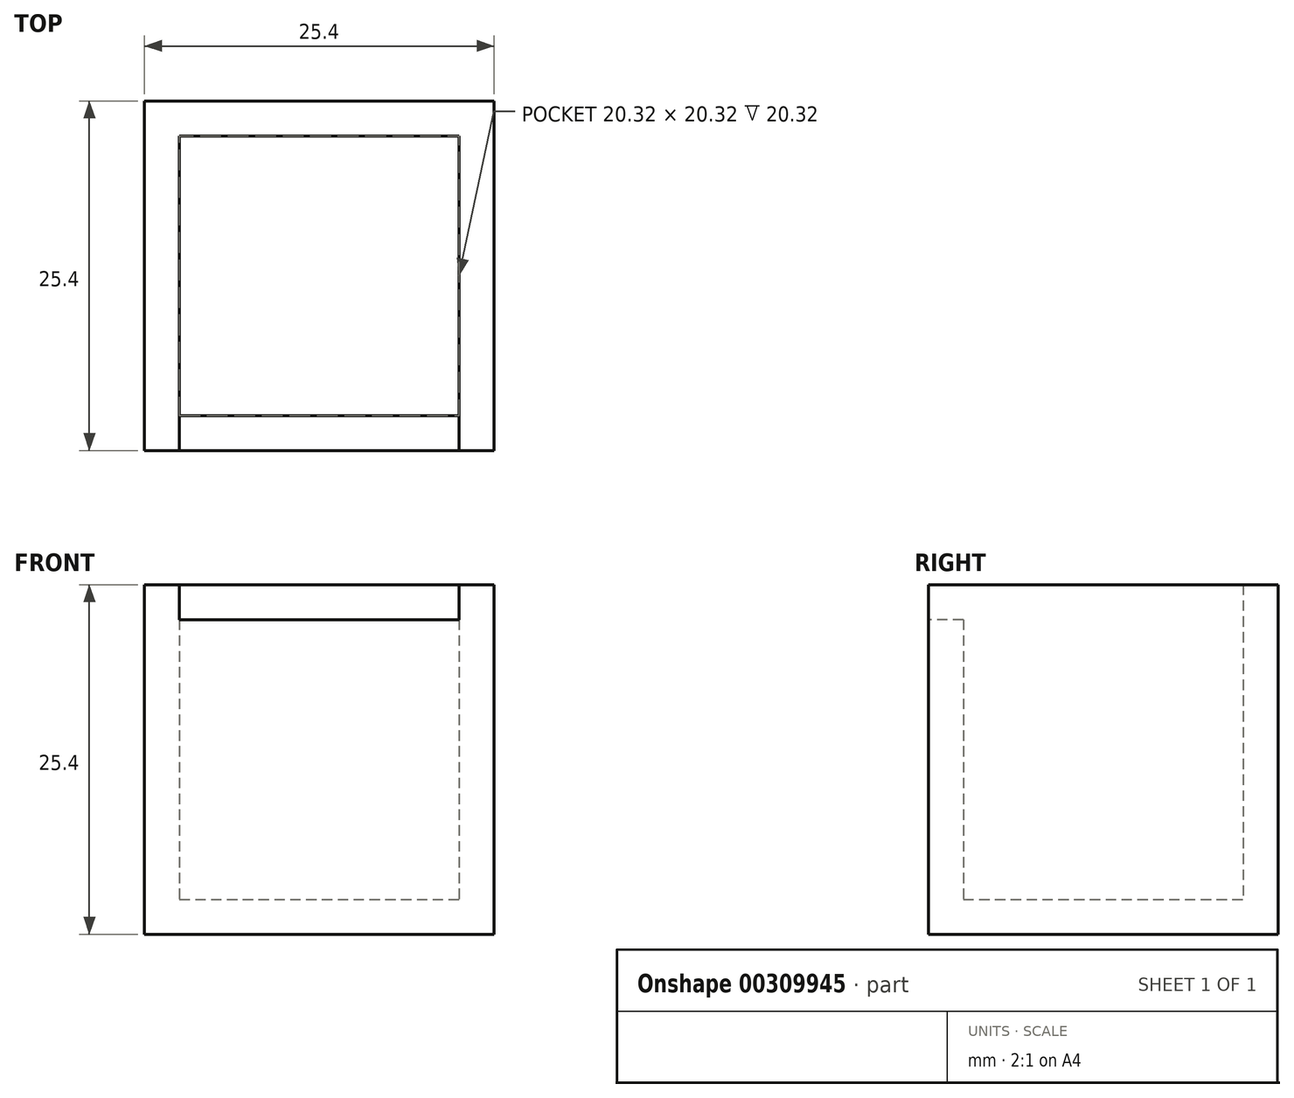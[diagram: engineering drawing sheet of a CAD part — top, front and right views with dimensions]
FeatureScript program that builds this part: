
annotation { "Feature Type Name" : "Feature", "Feature Type Description" : "" }
export const myFeature = defineFeature(function(context is Context, id is Id, definition is map)
    precondition{}
    {
        {
            var Q0;
            Q0=qCreatedBy(makeId("Front.planeOp"),FACE);
            var sketch = newSketch(context, id + "F0", { "sketchPlane" : qUnion([Q0])});
            skLineSegment(sketch, "E0.bottom", {"start": v(-12.7, 11.43) * mm, "end": v(12.7, 11.43) * mm});
            skLineSegment(sketch, "E0.top", {"start": v(-12.7, -11.43) * mm, "end": v(12.7, -11.43) * mm});
            skLineSegment(sketch, "E0.left", {"start": v(-12.7, 11.43) * mm, "end": v(-12.7, -11.43) * mm});
            skLineSegment(sketch, "E0.right", {"start": v(12.7, 11.43) * mm, "end": v(12.7, -11.43) * mm});
            skPoint(sketch, "E0.middle", {"position": v(0, 0) * mm});
            skSolve(sketch);
        }
        {
            var Q0;
            Q0=makeQuery(id+"F0.imprint","IMPRINT",FACE,{"disambiguationData":[TD([[makeQuery(id+"F0.imprint","IMPRINT",EDGE,{"derivedFrom":sQuery(id+"F0.wireOp",EDGE,"E0.bottom")}),-1.0]])]});
            extrude(context, id + "F1", {"entities" : qUnion([Q0]), "depth" : 25.4 * mm});
        }
        {
            var Q0;
            Q0=makeQuery(id+"F1.opExtrude","SWEPT_FACE",FACE,{"disambiguationData":[OSD([sQuery(id+"F0.wireOp",EDGE,"E0.bottom")])]});
            shell(context, id + "F2", {"entities" : qUnion([Q0]), "thickness" : 2.54 * mm});
        }
        {
            var Q0;
            Q0=makeQuery(id+"F1.opExtrude","SWEPT_FACE",FACE,{"disambiguationData":[OSD([sQuery(id+"F0.wireOp",EDGE,"E0.bottom")])]});
            var sketch = newSketch(context, id + "F3", { "sketchPlane" : qUnion([Q0])});
            skLineSegment(sketch, "E1.bottom", {"start": v(-12.7, 0) * mm, "end": v(12.7, 0) * mm});
            skLineSegment(sketch, "E1.top", {"start": v(-12.7, -25.4) * mm, "end": v(12.7, -25.4) * mm});
            skLineSegment(sketch, "E1.left", {"start": v(-12.7, 0) * mm, "end": v(-12.7, -25.4) * mm});
            skLineSegment(sketch, "E1.right", {"start": v(12.7, 0) * mm, "end": v(12.7, -25.4) * mm});
            skLineSegment(sketch, "E2", {"start": v(-10.16, -2.54) * mm, "end": v(-10.16, -25.4) * mm});
            skLineSegment(sketch, "E3", {"start": v(-10.16, -25.4) * mm, "end": v(-12.7, -25.4) * mm});
            skLineSegment(sketch, "E4", {"start": v(-10.16, -2.54) * mm, "end": v(10.16, -2.54) * mm});
            skLineSegment(sketch, "E5", {"start": v(10.16, -2.54) * mm, "end": v(10.16, -25.4) * mm});
            skLineSegment(sketch, "E6", {"start": v(10.16, -25.4) * mm, "end": v(12.7, -25.4) * mm});
            skSolve(sketch);
        }
        {
            var Q0;
            Q0=makeQuery(id+"F3.imprint","IMPRINT",FACE,{"disambiguationData":[TD([[makeQuery(id+"F3.imprint","IMPRINT",EDGE,{"derivedFrom":sQuery(id+"F3.wireOp",EDGE,"E1.bottom")}),-1.0]])]});
            extrude(context, id + "F4", {"entities" : qUnion([Q0]), "operationType" : NewBodyOperationType.ADD, "depth" : 2.54 * mm});
        }
    });
